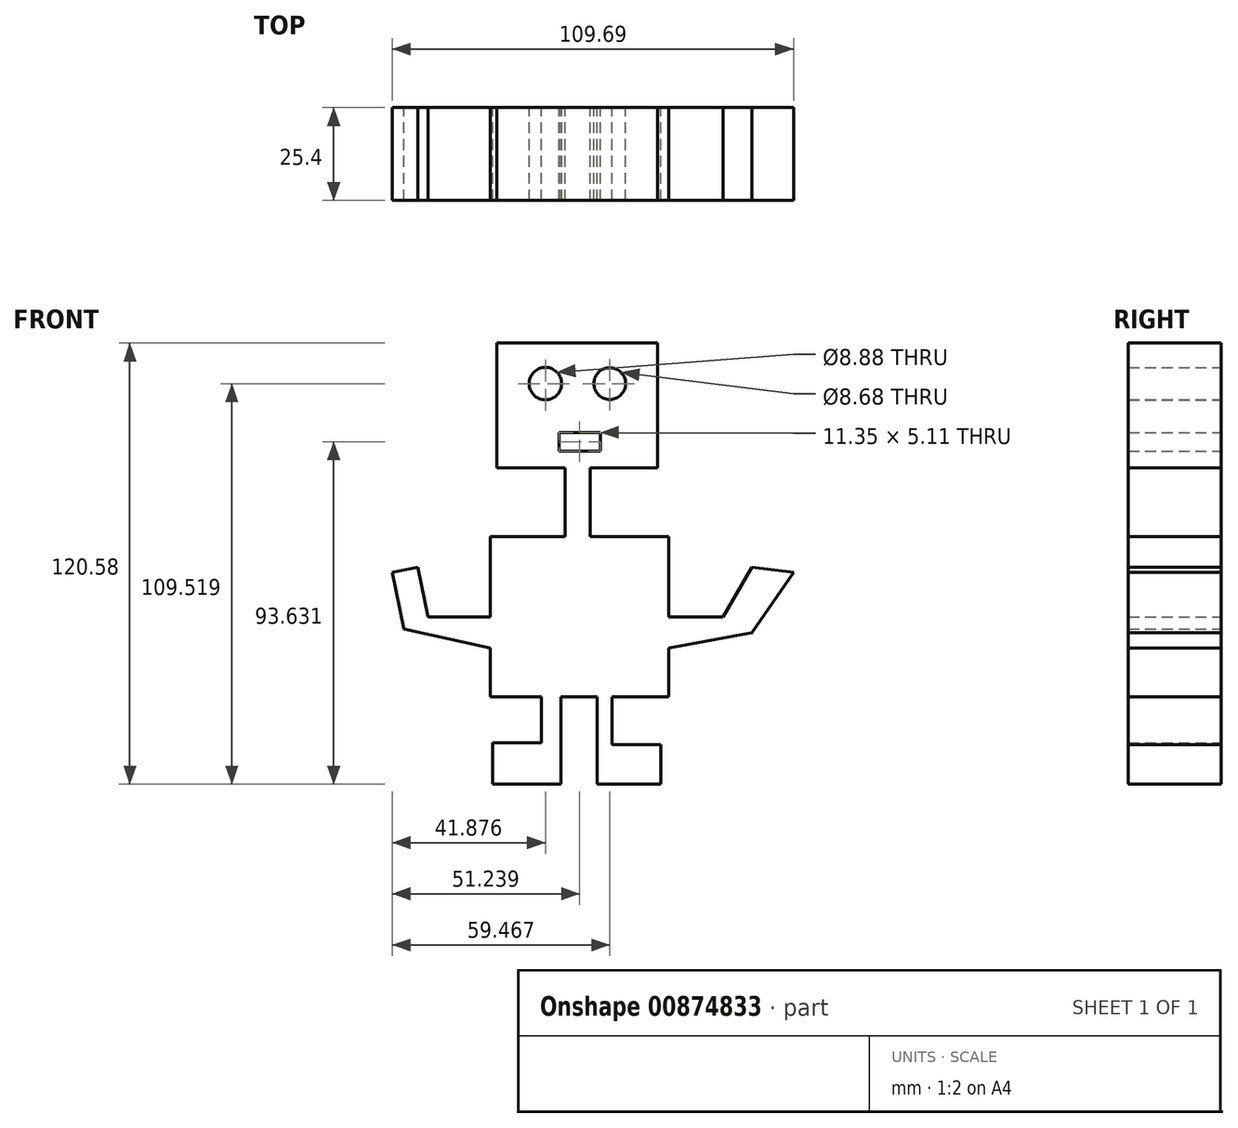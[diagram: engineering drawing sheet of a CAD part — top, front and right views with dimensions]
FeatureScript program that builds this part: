
annotation { "Feature Type Name" : "Feature", "Feature Type Description" : "" }
export const myFeature = defineFeature(function(context is Context, id is Id, definition is map)
    precondition{}
    {
        {
            var Q0;
            Q0=qCreatedBy(makeId("Front.planeOp"),FACE);
            var sketch = newSketch(context, id + "F0", { "sketchPlane" : qUnion([Q0])});
            skLineSegment(sketch, "E0.bottom", {"start": v(-21.99, 52.91) * mm, "end": v(21.99, 52.91) * mm});
            skLineSegment(sketch, "E0.top", {"start": v(-21.99, 18.87) * mm, "end": v(21.99, 18.87) * mm});
            skLineSegment(sketch, "E0.left", {"start": v(-21.99, 52.91) * mm, "end": v(-21.99, 18.87) * mm});
            skLineSegment(sketch, "E0.right", {"start": v(21.99, 52.91) * mm, "end": v(21.99, 18.87) * mm});
            skLineSegment(sketch, "E1", {"start": v(-3.26, 18.87) * mm, "end": v(-3.26, 0) * mm});
            skLineSegment(sketch, "E2", {"start": v(3.55, 18.87) * mm, "end": v(3.55, 0) * mm});
            skLineSegment(sketch, "E3.bottom", {"start": v(-23.7, 0) * mm, "end": v(25.1, 0) * mm});
            skLineSegment(sketch, "E3.top", {"start": v(-23.7, -43.84) * mm, "end": v(25.1, -43.84) * mm});
            skLineSegment(sketch, "E3.left", {"start": v(-23.7, 0) * mm, "end": v(-23.7, -43.84) * mm});
            skLineSegment(sketch, "E3.right", {"start": v(25.1, 0) * mm, "end": v(25.1, -43.84) * mm});
            skLineSegment(sketch, "E4", {"start": v(-9.79, -43.84) * mm, "end": v(-9.79, -56.32) * mm});
            skLineSegment(sketch, "E5", {"start": v(9.5, -43.84) * mm, "end": v(9.5, -56.89) * mm});
            skLineSegment(sketch, "E6", {"start": v(9.5, -56.89) * mm, "end": v(22.84, -56.89) * mm});
            skLineSegment(sketch, "E7", {"start": v(22.84, -56.89) * mm, "end": v(22.84, -67.67) * mm});
            skLineSegment(sketch, "E8", {"start": v(22.84, -67.67) * mm, "end": v(5.53, -67.67) * mm});
            skLineSegment(sketch, "E9", {"start": v(5.53, -67.67) * mm, "end": v(5.53, -43.84) * mm});
            skLineSegment(sketch, "E10", {"start": v(-9.79, -56.32) * mm, "end": v(-23.12, -56.32) * mm});
            skLineSegment(sketch, "E11", {"start": v(-23.12, -56.32) * mm, "end": v(-23.12, -67.67) * mm});
            skLineSegment(sketch, "E12", {"start": v(-23.12, -67.67) * mm, "end": v(-4.4, -67.67) * mm});
            skLineSegment(sketch, "E13", {"start": v(-4.4, -67.67) * mm, "end": v(-4.4, -43.84) * mm});
            skLineSegment(sketch, "E14", {"start": v(-23.7, -21.92) * mm, "end": v(-40.71, -21.92) * mm});
            skLineSegment(sketch, "E15", {"start": v(-40.71, -21.92) * mm, "end": v(-43.55, -8.37) * mm});
            skLineSegment(sketch, "E16", {"start": v(-43.55, -8.37) * mm, "end": v(-50.53, -9.83) * mm});
            skLineSegment(sketch, "E17", {"start": v(-50.53, -9.83) * mm, "end": v(-47.3, -25.3) * mm});
            skLineSegment(sketch, "E18", {"start": v(-47.3, -25.3) * mm, "end": v(-23.7, -30.5) * mm});
            skLineSegment(sketch, "E19", {"start": v(25.1, -21.92) * mm, "end": v(39.86, -21.92) * mm});
            skLineSegment(sketch, "E20", {"start": v(39.86, -21.92) * mm, "end": v(47.8, -8.37) * mm});
            skLineSegment(sketch, "E21", {"start": v(47.8, -8.37) * mm, "end": v(59.16, -9.83) * mm});
            skLineSegment(sketch, "E22", {"start": v(59.16, -9.83) * mm, "end": v(47.8, -26.24) * mm});
            skLineSegment(sketch, "E23", {"start": v(47.8, -26.24) * mm, "end": v(25.1, -30.5) * mm});
            skCircle(sketch, "E24", {"center": v(-8.65, 41.85) * mm, "radius": 4.44 * mm});
            skCircle(sketch, "E25", {"center": v(8.94, 41.85) * mm, "radius": 4.34 * mm});
            skLineSegment(sketch, "E26.bottom", {"start": v(-4.97, 28.51) * mm, "end": v(6.38, 28.51) * mm});
            skLineSegment(sketch, "E26.top", {"start": v(-4.97, 23.4) * mm, "end": v(6.38, 23.4) * mm});
            skLineSegment(sketch, "E26.left", {"start": v(-4.97, 28.51) * mm, "end": v(-4.97, 23.4) * mm});
            skLineSegment(sketch, "E26.right", {"start": v(6.38, 28.51) * mm, "end": v(6.38, 23.4) * mm});
            skSolve(sketch);
        }
        {
            var Q0;
            Q0 = qSketchRegion(id + "F0", true);
            extrude(context, id + "F1", {"entities" : qUnion([Q0]), "depth" : 25.4 * mm, "offsetDistance" : 25.4 * mm});
        }
    });
